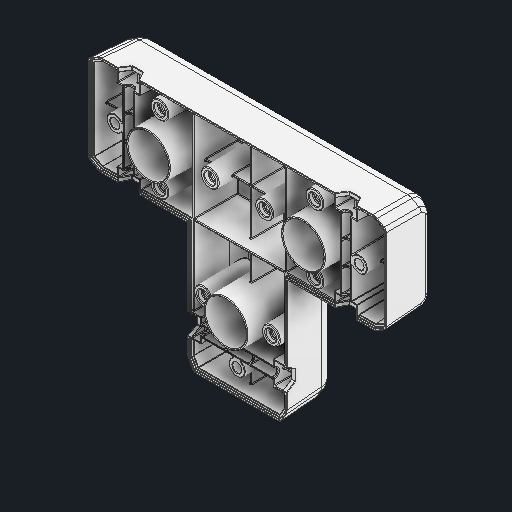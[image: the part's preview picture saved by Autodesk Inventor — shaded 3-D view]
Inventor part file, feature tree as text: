
AUTODESK INVENTOR PART (.ipt)
format: ipt  version: 2024.2 (Build 282272000, 272)  size: 4,938,240 bytes
history: native  units: in
note: dims shown in document units (in); Inventor stores cm internally (conversion verified against a paired STEP export)
features: fillet x1
ambient origin geometry x8: Origin, YZ Plane, XZ Plane, XY Plane, X Axis, Y Axis, Z Axis, Center Point
bodies: Solid1 (feature_tree)
feature tree (1):
  fillet  "Fillet31"  [1 undecoded]
note: 1 required parameter value undecoded (feature->parameter linkage not recoverable at this tier; creation-order binding heuristic only, values carry confidence <= 0.55)
